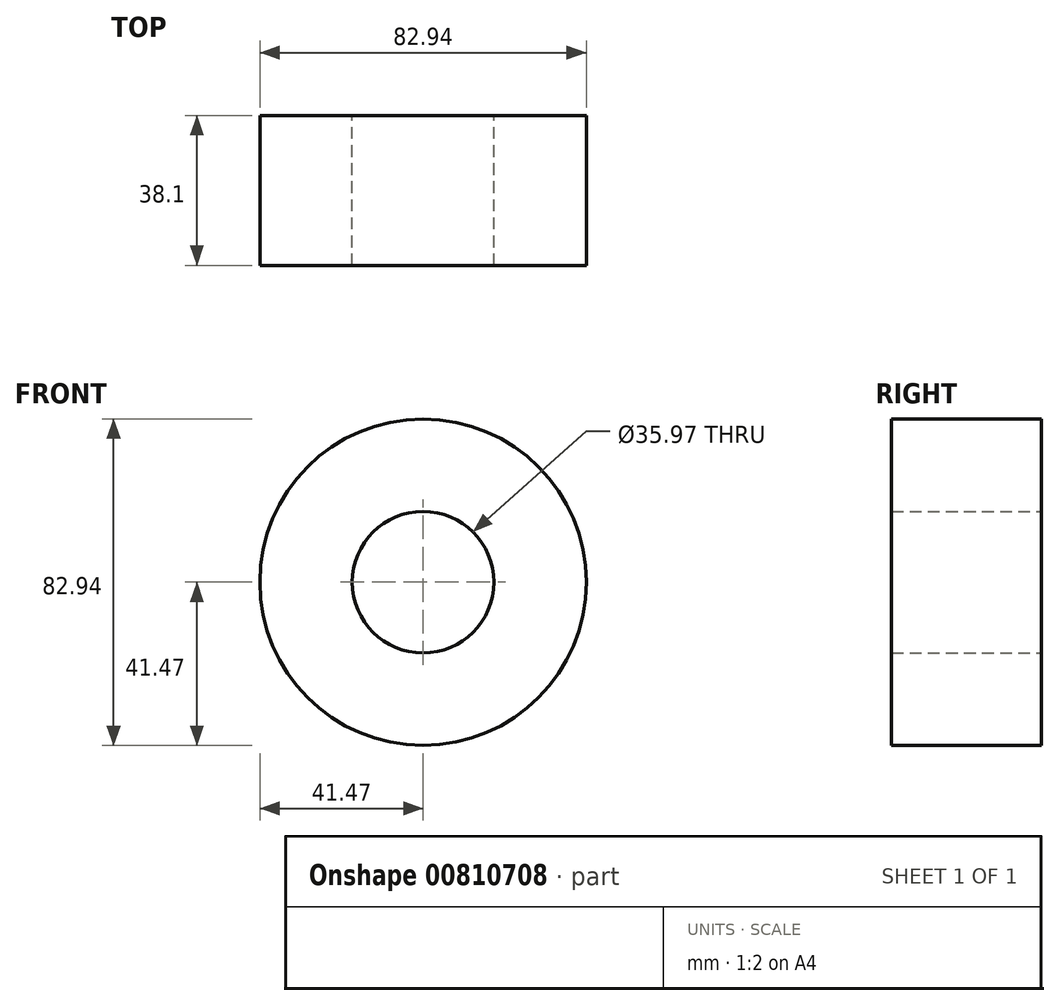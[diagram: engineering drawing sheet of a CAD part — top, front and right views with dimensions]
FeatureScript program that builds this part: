
annotation { "Feature Type Name" : "Feature", "Feature Type Description" : "" }
export const myFeature = defineFeature(function(context is Context, id is Id, definition is map)
    precondition{}
    {
        {
            var Q0;
            Q0=qCreatedBy(makeId("Front.planeOp"),FACE);
            var sketch = newSketch(context, id + "F0", { "sketchPlane" : qUnion([Q0])});
            skCircle(sketch, "E0", {"center": v(0, 0) * mm, "radius": 41.47 * mm});
            skCircle(sketch, "E1", {"center": v(0, 0) * mm, "radius": 17.98 * mm});
            skSolve(sketch);
        }
        {
            var Q0;
            Q0=qCreatedBy(makeId("Front.planeOp"),FACE);
            var sketch = newSketch(context, id + "F1", { "sketchPlane" : qUnion([Q0])});
            skSolve(sketch);
        }
        {
            var Q0;
            Q0 = qSketchRegion(id + "F1", true);
            var Q1;
            Q1=makeQuery(id+"F0.imprint","IMPRINT",FACE,{"disambiguationData":[TD([[makeQuery(id+"F0.imprint","IMPRINT",EDGE,{"derivedFrom":sQuery(id+"F0.wireOp",EDGE,"E0")}),1.0]])]});
            extrude(context, id + "F2", {"entities" : qUnion([Q0, Q1]), "depth" : 38.1 * mm, "offsetDistance" : 25.4 * mm});
        }
    });
